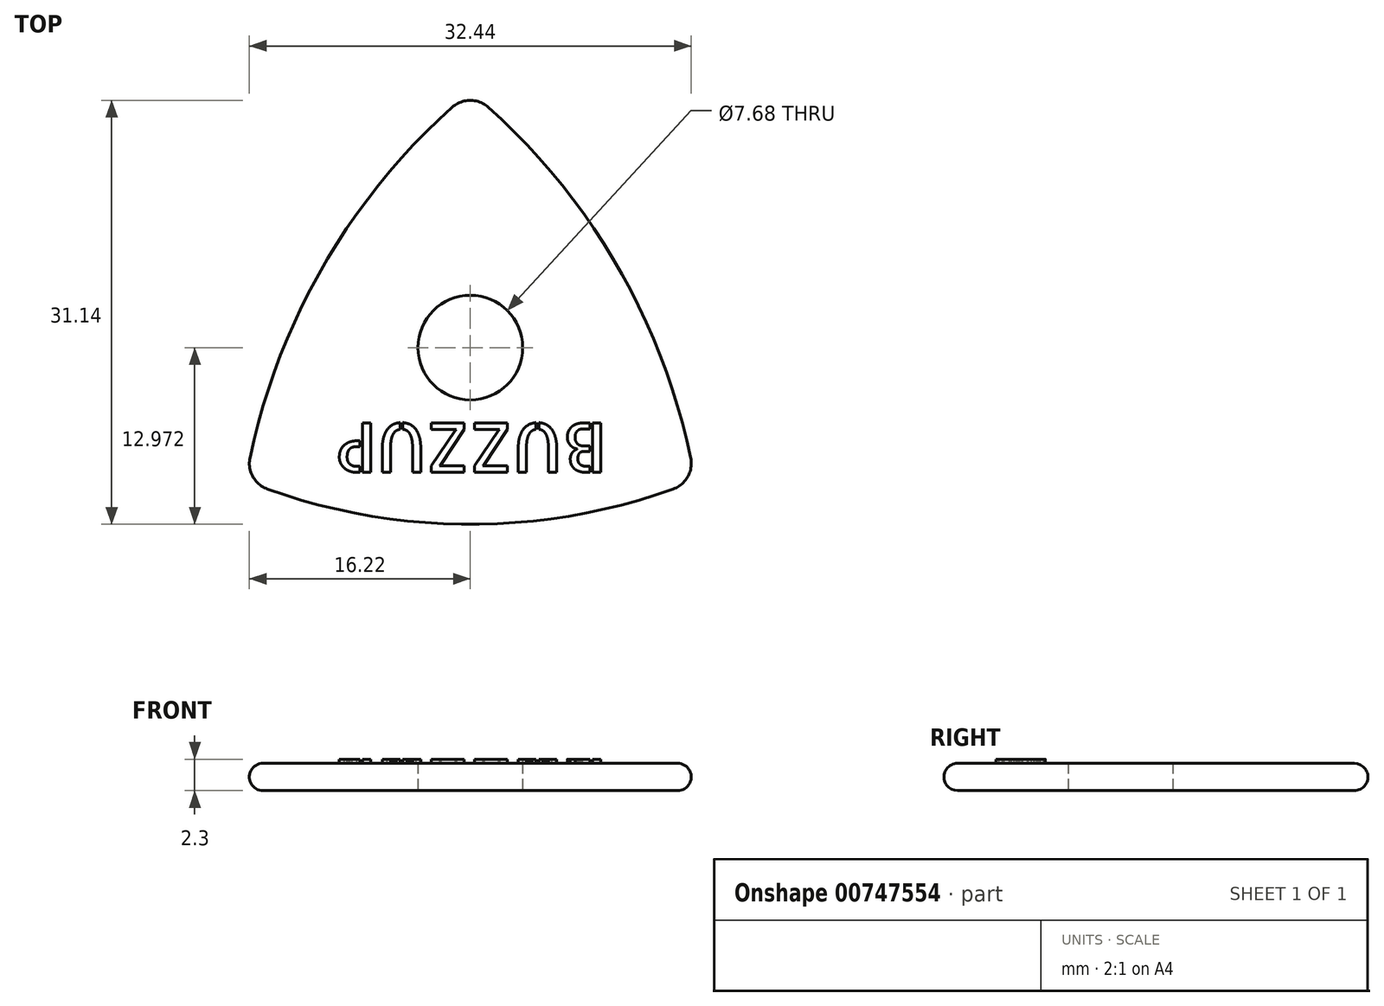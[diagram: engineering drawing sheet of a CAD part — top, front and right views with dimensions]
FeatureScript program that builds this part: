
annotation { "Feature Type Name" : "Feature", "Feature Type Description" : "" }
export const myFeature = defineFeature(function(context is Context, id is Id, definition is map)
    precondition{}
    {
        {
            var Q0;
            Q0=qCreatedBy(makeId("Top.planeOp"),FACE);
            var sketch = newSketch(context, id + "F0", { "sketchPlane" : qUnion([Q0])});
            skArc(sketch, "E0", {"start": v(0, 28.58) * mm, "mid": v(-10.8, 15.76) * mm, "end": v(-16.5, 0) * mm});
            skArc(sketch, "E1.MirrorCS", {"start": v(0, 28.58) * mm, "mid": v(10.8, 15.76) * mm, "end": v(16.5, 0) * mm});
            skArc(sketch, "E2", {"start": v(-16.5, 0) * mm, "mid": v(0, -3.2) * mm, "end": v(16.5, 0) * mm});
            skPoint(sketch, "E3", {"position": v(0, 9.77) * mm});
            skCircle(sketch, "E4", {"center": v(0, 9.77) * mm, "radius": 3.84 * mm});
            skCircle(sketch, "E5", {"center": v(0, 9.77) * mm, "radius": 2.57 * mm});
            skCircle(sketch, "E6", {"center": v(0, 9.77) * mm, "radius": 1.47 * mm});
            skSolve(sketch);
        }
        {
            var Q0;
            Q0=makeQuery(id+"F0.imprint","IMPRINT",FACE,{"disambiguationData":[TD([[makeQuery(id+"F0.imprint","IMPRINT",EDGE,{"derivedFrom":sQuery(id+"F0.wireOp",EDGE,"E0")}),1.0]])]});
            extrude(context, id + "F1", {"entities" : qUnion([Q0]), "depth" : 2 * mm, "offsetDistance" : 25 * mm});
        }
        {
            var Q0;
            Q0=makeQuery(id+"F1.opExtrude","SWEPT_EDGE",EDGE,{"disambiguationData":[OSD([sQuery(id+"F0.wireOp",EDGE,"E1.MirrorCS"),sQuery(id+"F0.wireOp",EDGE,"E2")])]});
            var Q1;
            Q1=makeQuery(id+"F1.opExtrude","SWEPT_EDGE",EDGE,{"disambiguationData":[OSD([sQuery(id+"F0.wireOp",EDGE,"E0"),sQuery(id+"F0.wireOp",EDGE,"E1.MirrorCS")])]});
            var Q2;
            Q2=makeQuery(id+"F1.opExtrude","SWEPT_EDGE",EDGE,{"disambiguationData":[OSD([sQuery(id+"F0.wireOp",EDGE,"E0"),sQuery(id+"F0.wireOp",EDGE,"E2")])]});
            fillet(context, id + "F2", {"entities" : qUnion([Q0, Q1, Q2]), "radius" : 2 * mm, "tangentPropagation" : true, "allowEdgeOverflow" : false});
        }
        {
            var Q0;
            Q0=makeQuery(id+"F1.opExtrude","SWEPT_FACE",FACE,{"disambiguationData":[OSD([sQuery(id+"F0.wireOp",EDGE,"E2")])]});
            var Q1;
            Q1=makeQuery(id+"F1.opExtrude","SWEPT_FACE",FACE,{"disambiguationData":[OSD([sQuery(id+"F0.wireOp",EDGE,"E0")])]});
            var Q2;
            Q2=makeQuery(id+"F1.opExtrude","SWEPT_FACE",FACE,{"disambiguationData":[OSD([sQuery(id+"F0.wireOp",EDGE,"E1.MirrorCS")])]});
            fillet(context, id + "F3", {"entities" : qUnion([Q0, Q1, Q2]), "radius" : 1 * mm, "tangentPropagation" : true, "allowEdgeOverflow" : false});
        }
        {
            var Q0;
            Q0=qCreatedBy(makeId("Top.planeOp"),FACE);
            var sketch = newSketch(context, id + "F4", { "sketchPlane" : qUnion([Q0])});
            skText(sketch, "E7", { "text": "BUZZUP", "fontName": "AllertaStencil-Regular.ttf"});
            const initialGuessF4  = {"E7": [0.01005, 0.00424, -1, 0, 0.00363]};
            skSetInitialGuess(sketch, initialGuessF4);
            skSolve(sketch);
        }
        {
            var Q0;
            Q0 = qSketchRegion(id + "F4", true);
            extrude(context, id + "F5", {"entities" : qUnion([Q0]), "operationType" : NewBodyOperationType.ADD, "depth" : 2.3 * mm, "offsetDistance" : 25 * mm});
        }
    });
